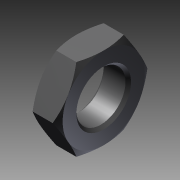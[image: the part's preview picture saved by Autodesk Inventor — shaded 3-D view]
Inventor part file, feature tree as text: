
AUTODESK INVENTOR PART (.ipt)
format: ipt  version: 2011 SP1 (Build 150282100, 282)  size: 121,344 bytes
history: native  units: mm
features: other x7, sketch x3, revolve x2, extrude x1
ambient origin geometry x8: Origin, YZ Plane, XZ Plane, XY Plane, X Axis, Y Axis, Z Axis, Center Point
bodies: Solid1 (feature_tree)
feature tree (13):
  revolve  "Revolution1"  Angle=360.0deg
  revolve  "Revolution2"  [1 undecoded]
  extrude  "Extrusion1"  [1 undecoded]
  other  "GIE1_XY"
  other  "GIE1_YZ"
  other  "GIE1_ZX"
  other  "GIE1_X"
  other  "GIE1_Y"
  other  "GIE1_Z"
  other  "GIE1_Center"
  sketch  "Skizze_1"  dims[d0=360.0deg d1=360.0deg]
  sketch  "Skizze_2_ALT_Drilling_1"  dims[d2=8.0mm d3=0.0mm d4=0.0mm]
  sketch  "Skizze_3"
note: 2 required parameter values undecoded (feature->parameter linkage not recoverable at this tier; creation-order binding heuristic only, values carry confidence <= 0.55)